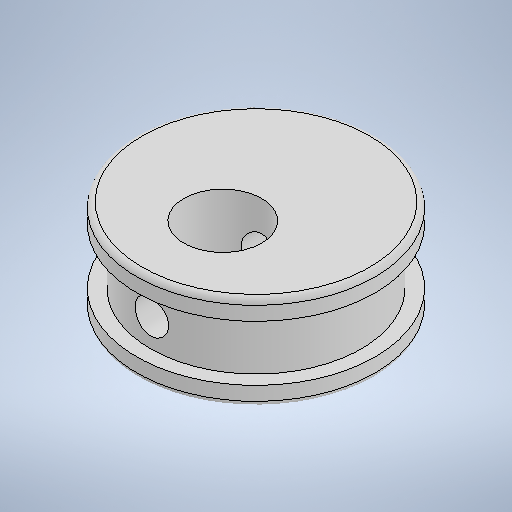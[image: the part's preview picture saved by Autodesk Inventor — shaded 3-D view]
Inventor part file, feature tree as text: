
AUTODESK INVENTOR PART (.ipt)
format: ipt  version: 2025 (Build 290162010, 162A)  size: 288,256 bytes
history: native  units: mm
features: sketch x3, revolve x1, hole x1, fillet x1, plane x1, extrude x1
ambient origin geometry x8: Origin, YZ Plane, XZ Plane, XY Plane, X Axis, Y Axis, Z Axis, Center Point
bodies: Solid1 (feature_tree)
feature tree (8):
  revolve  "Revolution1"  [1 undecoded]
  hole  "Hole1"  [1 undecoded]
  fillet  "Fillet1"  Radius=43.0mm
  plane  "Work Plane1"
  extrude  "Extrusion1"  Depth=10.0mm
  sketch  "Sketch1"  dims[d1=3.5mm d2=3.5mm]
  sketch  "Sketch2"  dims[d3=17.0mm d4=38.0mm d5=43.0mm]
  sketch  "Sketch4"  dims[d6=90.0deg d7=14.0mm d8=10.0mm d9=4.0mm d10=2.0mm d11=90.0deg d12=8.0mm d13=0.0mm d14=6.0mm d15=1.0mm d16=20.0mm d17=6.0mm d18=10.0mm d19=0.0mm]
note: 2 required parameter values undecoded (feature->parameter linkage not recoverable at this tier; creation-order binding heuristic only, values carry confidence <= 0.55)